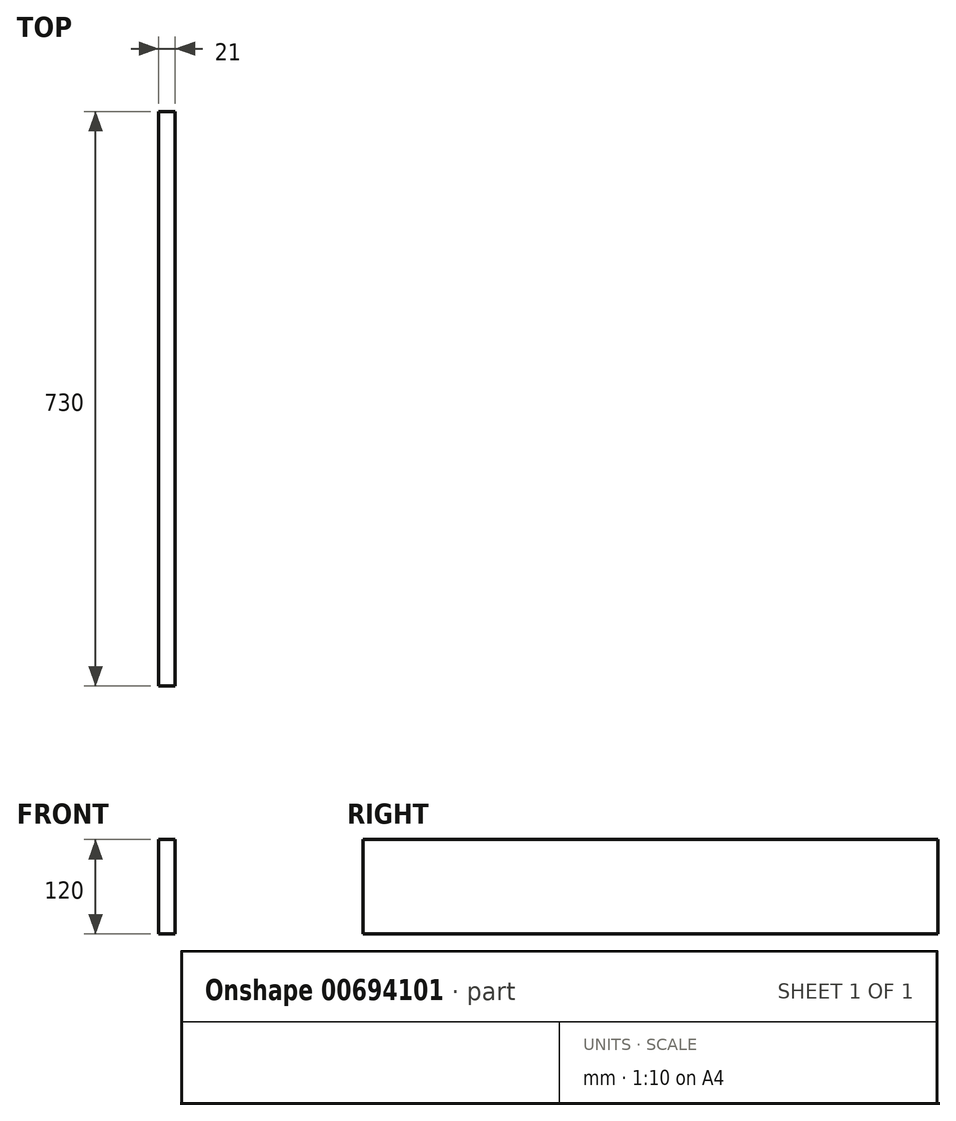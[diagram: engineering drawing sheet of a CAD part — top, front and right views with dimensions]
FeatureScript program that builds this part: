
annotation { "Feature Type Name" : "Feature", "Feature Type Description" : "" }
export const myFeature = defineFeature(function(context is Context, id is Id, definition is map)
    precondition{}
    {
        {
            var Q0;
            Q0=qCreatedBy(makeId("Right.planeOp"),FACE);
            var sketch = newSketch(context, id + "F0", { "sketchPlane" : qUnion([Q0])});
            skLineSegment(sketch, "E0.bottom", {"start": v(-365, -60) * mm, "end": v(365, -60) * mm});
            skLineSegment(sketch, "E0.top", {"start": v(-365, 60) * mm, "end": v(365, 60) * mm});
            skLineSegment(sketch, "E0.left", {"start": v(-365, -60) * mm, "end": v(-365, 60) * mm});
            skLineSegment(sketch, "E0.right", {"start": v(365, -60) * mm, "end": v(365, 60) * mm});
            skSolve(sketch);
        }
        {
            var Q0;
            Q0=makeQuery(id+"F0.imprint","IMPRINT",FACE,{"disambiguationData":[TD([[makeQuery(id+"F0.imprint","IMPRINT",EDGE,{"derivedFrom":sQuery(id+"F0.wireOp",EDGE,"E0.bottom")}),1.0]])]});
            extrude(context, id + "F1", {"entities" : qUnion([Q0]), "depth" : 21 * mm, "offsetDistance" : 25 * mm});
        }
    });
